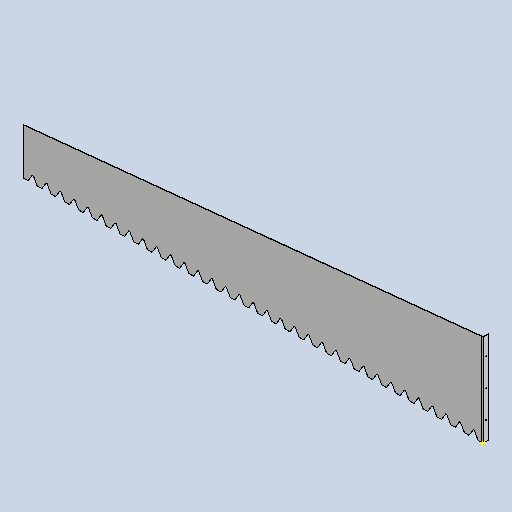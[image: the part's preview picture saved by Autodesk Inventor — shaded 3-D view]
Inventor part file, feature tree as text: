
AUTODESK INVENTOR PART (.ipt)
format: ipt  version: 2025 (Build 290162010, 162A)  size: 645,120 bytes
history: native  units: mm
features: other x5, sketch x3
ambient origin geometry x8: Origin, YZ Plane, XZ Plane, XY Plane, X Axis, Y Axis, Z Axis, Center Point
bodies: Solid1 (feature_tree)
feature tree (8):
  other  "MSC 071 ridge 1.ipt"
  sketch  "Sketch5"
  other  "A-Side Definition"
  other  "Solid1::MSC 071 ridge 1.ipt"
  other  "TaggingFeature1"
  sketch  "Sketch1"  dims[d0=10.0mm]
  sketch  "Sketch4"  dims[d1=2.0mm]
  other  "Definition1"
